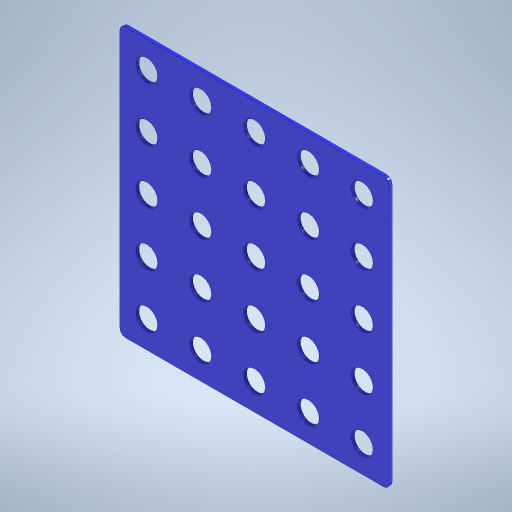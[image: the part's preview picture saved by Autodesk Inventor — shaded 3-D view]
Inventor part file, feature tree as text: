
AUTODESK INVENTOR PART (.ipt)
format: ipt  version: 2024 (Build 280153000, 153)  size: 292,864 bytes
history: native  units: mm
features: fillet x3, extrude x2, sketch x2, other x1, pattern_linear x1
ambient origin geometry x8: Origin, YZ Plane, XZ Plane, XY Plane, X Axis, Y Axis, Z Axis, Center Point
bodies: Body1 (feature_tree)
feature tree (9):
  other  "Těleso1"
  extrude  "Vysunutí1"  Depth=50.0mm
  extrude  "Vysunutí2"  Depth=50.0mm
  pattern_linear  "Obdélníkové pole1"  Spacing1=10.0mm  [1 undecoded]
  fillet  "Zaoblení1"  Radius=10.0mm
  fillet  "Zaoblení2"  Radius=0.5mm
  fillet  "Zaoblení3"  Radius=4.0mm
  sketch  "Náčrt1"
  sketch  "Náčrt2"
note: 1 required parameter value undecoded (feature->parameter linkage not recoverable at this tier; creation-order binding heuristic only, values carry confidence <= 0.55)
